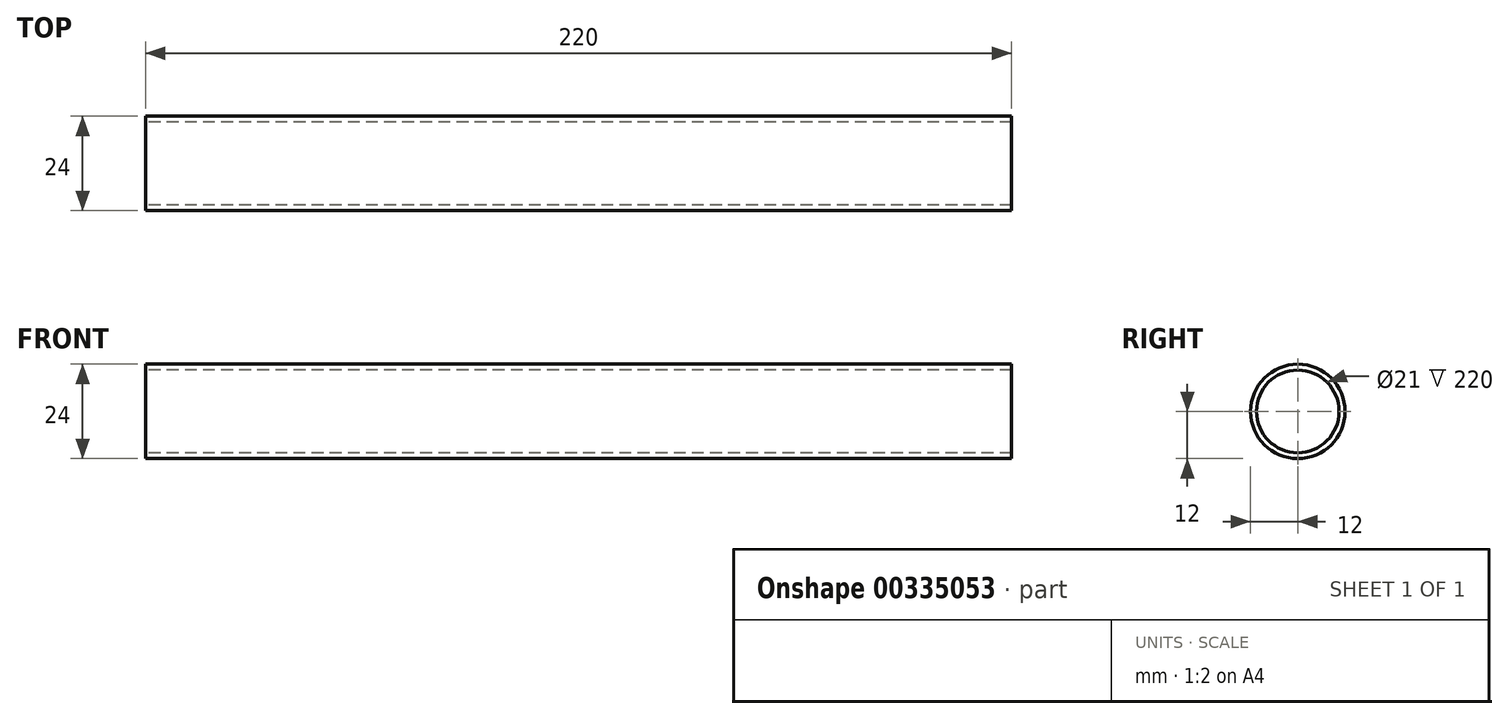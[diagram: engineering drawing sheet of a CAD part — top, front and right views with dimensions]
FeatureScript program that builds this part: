
annotation { "Feature Type Name" : "Feature", "Feature Type Description" : "" }
export const myFeature = defineFeature(function(context is Context, id is Id, definition is map)
    precondition{}
    {
        {
            var Q0;
            Q0=qCreatedBy(makeId("Right.planeOp"),FACE);
            var sketch = newSketch(context, id + "F0", { "sketchPlane" : qUnion([Q0])});
            skCircle(sketch, "E0", {"center": v(0, 0) * mm, "radius": 12 * mm});
            skCircle(sketch, "E1", {"center": v(0, 0) * mm, "radius": 10.5 * mm});
            skSolve(sketch);
        }
        {
            var Q0;
            Q0=makeQuery(id+"F0.imprint","IMPRINT",FACE,{"disambiguationData":[TD([[makeQuery(id+"F0.imprint","IMPRINT",EDGE,{"derivedFrom":sQuery(id+"F0.wireOp",EDGE,"E0")}),1.0]])]});
            extrude(context, id + "F1", {"entities" : qUnion([Q0]), "depth" : 220 * mm});
        }
    });
